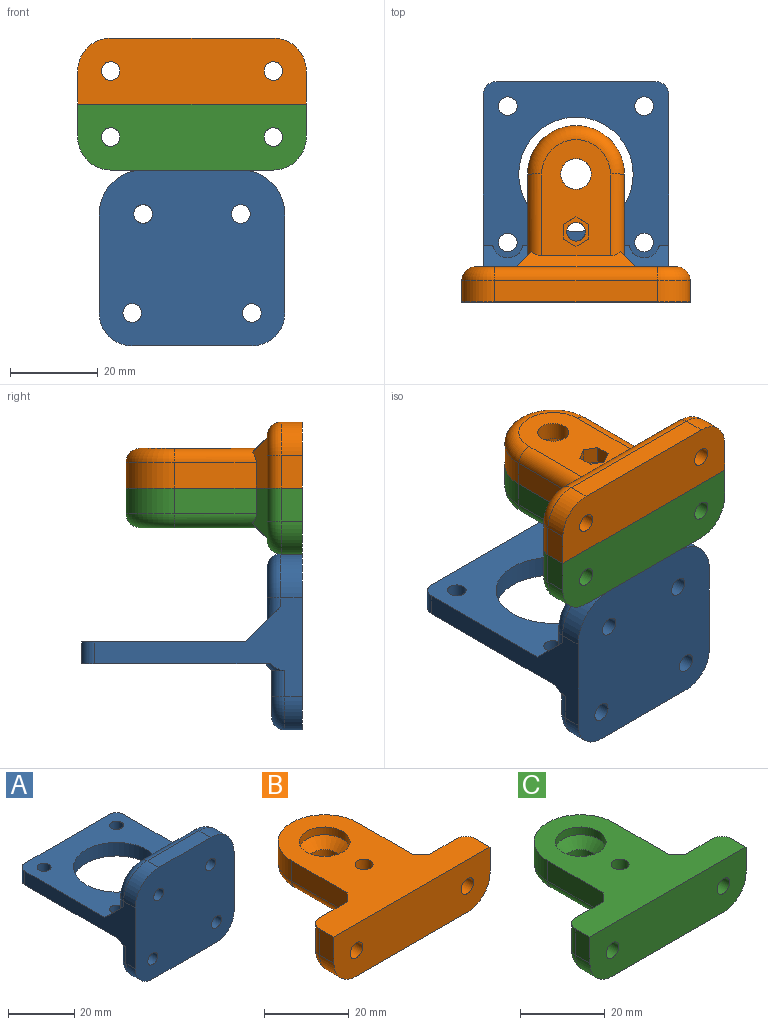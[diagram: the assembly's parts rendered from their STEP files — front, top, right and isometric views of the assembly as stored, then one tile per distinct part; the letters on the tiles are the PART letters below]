
ASSEMBLY  parts=3 mates=4
PART A: 59 faces, bbox 45.2x50.2x41.4 mm
  f0: plane 36.2x10.5mm, normal (0,1,0), area 294.4mm2, adj f27,f28,f44,f45,f46,f47,f48,f57
  f1: plane 36.2x12mm, normal (0,1,0), area 354.4mm2, adj f9,f31,f32,f33,f34,f35,f36,f37
  f2: cylinder r=2.12mm len=4.25mm, axis (0,1,0), area 53.4mm2, adj f6,f43
  f3: cylinder r=2.12mm len=4.25mm, axis (0,1,0), area 53.4mm2, adj f6,f30
  f4: cylinder r=2.12mm len=4.25mm, axis (0,1,0), area 53.4mm2, adj f6,f29
  f5: cylinder r=2.12mm len=4.25mm, axis (0,1,0), area 53.4mm2, adj f6,f26
  f6: plane 42.2x40mm, normal (0,-1,0), area 1564.2mm2, adj f2,f3,f4,f5,f10,f12,f18,f19
  f7: cylinder r=2.12mm len=5mm, axis (0,0,-1), area 66.8mm2, adj f16,f17
  f8: cylinder r=2.12mm len=5mm, axis (0,0,-1), area 66.8mm2, adj f16,f17
  f9: plane 42.2x8mm, normal (0,0.71,0.71), area 261.3mm2, adj f1,f10,f12,f16,f21,f22,f49,f53
  f10: plane 47.2x22.5mm, normal (1,0,0), area 351.2mm2, adj f6,f9,f16,f17,f19,f24,f48,f53
  f11: plane 36.2x5mm, normal (0,1,0), area 181mm2, adj f16,f17,f54,f55
  f12: plane 47.2x22.5mm, normal (-1,0,0), area 351.2mm2, adj f6,f9,f16,f17,f20,f25,f44,f49
  f13: cylinder r=13mm len=26mm, axis (0,0,-1), area 408.4mm2, adj f16,f17
  f14: cylinder r=2.12mm len=5mm, axis (0,0,-1), area 66.8mm2, adj f16,f17
  f15: cylinder r=2.12mm len=5mm, axis (0,0,-1), area 66.8mm2, adj f16,f17
  f16: plane 42.2x40.1mm, normal (0,0,1), area 1008.4mm2, adj f7,f8,f9,f10,f11,f12,f13,f14
  f17: plane 42.85x42.2mm, normal (0,0,-1), area 1170.4mm2, adj f7,f8,f10,f11,f12,f13,f14,f15
  f18: plane 22.2x5mm, normal (0,0,1), area 111mm2, adj f6,f19,f20,f51
  f19: cylinder r=10mm len=10mm, axis (0,1,0), area 78.5mm2, adj f6,f10,f18,f52
  f20: cylinder r=10mm len=10mm, axis (0,-1,0), area 78.5mm2, adj f6,f12,f18,f50
  f21: cylinder r=3.5mm len=6.9mm, axis (0,0,-1), area 18.3mm2, adj f9,f16
  f22: cylinder r=3.5mm len=6.9mm, axis (0,0,-1), area 18.3mm2, adj f9,f16
  f23: plane 27.2x4mm, normal (0,0,-1), area 108.8mm2, adj f6,f24,f25,f46
  f24: cylinder r=7.5mm len=7.5mm, axis (0,-1,0), area 47.1mm2, adj f6,f10,f23,f47
  f25: cylinder r=7.5mm len=7.5mm, axis (0,1,0), area 47.1mm2, adj f6,f12,f23,f45
  f26: plane 7x7mm, normal (0,1,0), area 24.3mm2, adj f5,f27
  f27: cylinder r=3.5mm len=7mm, axis (0,1,0), area 66mm2, adj f0,f26
  f28: cylinder r=3.5mm len=7mm, axis (0,1,0), area 66mm2, adj f0,f29
  f29: plane 7x7mm, normal (0,1,0), area 24.3mm2, adj f4,f28
  f30: plane 6.74x5.84mm, normal (0,1,0), area 15.3mm2, adj f3,f31,f32,f33,f34,f35,f36
  f31: plane 4x2.92mm, normal (-0.5,0,0.87), area 13.5mm2, adj f1,f30,f32,f36
  f32: plane 4x2.92mm, normal (0.5,0,0.87), area 13.5mm2, adj f1,f30,f31,f33
  f33: plane 4x3.37mm, normal (1,0,0), area 13.5mm2, adj f1,f30,f32,f34
  f34: plane 4x2.92mm, normal (0.5,0,-0.87), area 13.5mm2, adj f1,f30,f33,f35
  f35: plane 4x2.92mm, normal (-0.5,0,-0.87), area 13.5mm2, adj f1,f30,f34,f36
  f36: plane 4x3.37mm, normal (-1,0,0), area 13.5mm2, adj f1,f30,f31,f35
  f37: plane 4x2.92mm, normal (-0.5,0,0.87), area 13.5mm2, adj f1,f38,f42,f43
  f38: plane 4x2.92mm, normal (0.5,0,0.87), area 13.5mm2, adj f1,f37,f39,f43
  f39: plane 4x3.37mm, normal (1,0,0), area 13.5mm2, adj f1,f38,f40,f43
  f40: plane 4x2.92mm, normal (0.5,0,-0.87), area 13.5mm2, adj f1,f39,f41,f43
  f41: plane 4x2.92mm, normal (-0.5,0,-0.87), area 13.5mm2, adj f1,f40,f42,f43
  f42: plane 4x3.37mm, normal (-1,0,0), area 13.5mm2, adj f1,f37,f41,f43
  f43: plane 6.74x5.84mm, normal (0,1,0), area 15.3mm2, adj f2,f37,f38,f39,f40,f41,f42
  f44: cylinder r=3mm len=6mm, axis (0,0,1), area 28.3mm2, adj f0,f12,f45,f56
  f45: torus R=4.5mm, axis (0,1,0), area 47.4mm2, adj f0,f25,f44,f46
  f46: cylinder r=3mm len=27.2mm, axis (-1,0,0), area 128.2mm2, adj f0,f23,f45,f47
  f47: torus R=4.5mm, axis (0,1,0), area 47.4mm2, adj f0,f24,f46,f48
  f48: cylinder r=3mm len=6mm, axis (0,0,-1), area 28.3mm2, adj f0,f10,f47,f58
  f49: cylinder r=3mm len=5mm, axis (0,0,1), area 18.4mm2, adj f1,f9,f12,f50
  f50: torus R=7mm, axis (0,-1,0), area 66mm2, adj f1,f20,f49,f51
  f51: cylinder r=3mm len=22.2mm, axis (-1,0,0), area 104.6mm2, adj f1,f18,f50,f52
  f52: torus R=7mm, axis (0,-1,0), area 66mm2, adj f1,f19,f51,f53
  f53: cylinder r=3mm len=5mm, axis (0,0,-1), area 18.4mm2, adj f1,f9,f10,f52
  f54: cylinder r=3mm len=5mm, axis (0,0,-1), area 23.6mm2, adj f10,f11,f16,f17
  f55: cylinder r=3mm len=5mm, axis (0,0,1), area 23.6mm2, adj f11,f12,f16,f17
  f56: cone r=4.5mm half-angle=45deg, axis (0,0,1), area 7.6mm2, adj f12,f17,f44,f57
  f57: plane 36.2x1.5mm, normal (0,0.71,-0.71), area 76.8mm2, adj f0,f17,f56,f58
  f58: cone r=4.5mm half-angle=45deg, axis (0,0,1), area 7.6mm2, adj f10,f17,f48,f57
PART B: 50 faces, bbox 53.2x41x15.6 mm
  f0: plane 45.6x11.8mm, normal (0,1,0), area 160.7mm2, adj f18,f23,f24,f25,f28,f29,f30,f31
  f1: cylinder r=2.12mm len=4.25mm, axis (0,-1,0), area 53.4mm2, adj f12,f35
  f2: cylinder r=2.12mm len=4.25mm, axis (0,-1,0), area 53.4mm2, adj f12,f34
  f3: cylinder r=3.5mm len=7mm, axis (0,0,-1), area 93.5mm2, adj f21,f22
  f4: plane 4x2.92mm, normal (-0.5,0.87,0), area 13.5mm2, adj f5,f9,f20,f21
  f5: plane 4x2.92mm, normal (0.5,0.87,0), area 13.5mm2, adj f4,f6,f20,f21
  f6: plane 4x3.37mm, normal (1,0,0), area 13.5mm2, adj f5,f7,f20,f21
  f7: plane 4x2.92mm, normal (0.5,-0.87,0), area 13.5mm2, adj f6,f8,f20,f21
  f8: plane 4x2.92mm, normal (-0.5,-0.87,0), area 13.5mm2, adj f7,f9,f20,f21
  f9: plane 4x3.37mm, normal (-1,0,0), area 13.5mm2, adj f4,f8,f20,f21
  f10: cylinder r=2.12mm len=5mm, axis (0,0,-1), area 66.8mm2, adj f18,f20
  f11: plane 37x4.8mm, normal (0,0,-1), area 177.6mm2, adj f12,f26,f27,f44
  f12: plane 52x15mm, normal (0,-1,0), area 727.5mm2, adj f1,f2,f11,f13,f17,f18,f26,f27
  f13: plane 7.5x4.8mm, normal (1,0,0), area 36mm2, adj f12,f18,f26,f46
  f14: plane 18.6x5.8mm, normal (1,0,0), area 107.9mm2, adj f15,f18,f24,f47
  f15: cylinder r=11mm len=22mm, axis (0,0,-1), area 200.4mm2, adj f14,f16,f18,f48
  f16: plane 18.6x5.8mm, normal (-1,0,0), area 107.9mm2, adj f15,f18,f23,f49
  f17: plane 7.5x4.8mm, normal (-1,0,0), area 36mm2, adj f12,f18,f27,f42
  f18: plane 52x40.1mm, normal (0,0,1), area 944.8mm2, adj f0,f10,f12,f13,f14,f15,f16,f17
  f19: cylinder r=6mm len=12mm, axis (0,0,1), area 84.8mm2, adj f18,f22
  f20: plane 6.74x5.84mm, normal (0,0,-1), area 15.3mm2, adj f4,f5,f6,f7,f8,f9,f10
  f21: plane 26.4x15.6mm, normal (0,0,-1), area 317.8mm2, adj f3,f4,f5,f6,f7,f8,f9,f25
  f22: cone r=3.5mm half-angle=45deg, axis (0,0,1), area 105.5mm2, adj f3,f19
  f23: plane 11.5x3.44mm, normal (-0.71,0.71,0), area 37.8mm2, adj f0,f16,f18,f25,f49
  f24: plane 11.5x3.44mm, normal (0.71,0.71,0), area 37.8mm2, adj f0,f14,f18,f25,f47
  f25: plane 27x3.44mm, normal (0,0.71,-0.71), area 89.7mm2, adj f0,f21,f23,f24,f47,f49
  f26: cylinder r=7.5mm len=7.5mm, axis (0,1,0), area 56.5mm2, adj f11,f12,f13,f45
  f27: cylinder r=7.5mm len=7.5mm, axis (0,-1,0), area 56.5mm2, adj f11,f12,f17,f43
  f28: plane 4x3.37mm, normal (-1,0,0), area 13.5mm2, adj f0,f29,f33,f34
  f29: plane 4x2.92mm, normal (-0.5,0,0.87), area 13.5mm2, adj f0,f28,f30,f34
  f30: plane 4x2.92mm, normal (0.5,0,0.87), area 13.5mm2, adj f0,f29,f31,f34
  f31: plane 4x3.37mm, normal (1,0,0), area 13.5mm2, adj f0,f30,f32,f34
  f32: plane 4x2.92mm, normal (0.5,0,-0.87), area 13.5mm2, adj f0,f31,f33,f34
  f33: plane 4x2.92mm, normal (-0.5,0,-0.87), area 13.5mm2, adj f0,f28,f32,f34
  f34: plane 6.74x5.84mm, normal (0,1,0), area 15.3mm2, adj f2,f28,f29,f30,f31,f32,f33
  f35: plane 6.74x5.84mm, normal (0,1,0), area 15.3mm2, adj f1,f36,f37,f38,f39,f40,f41
  f36: plane 4x2.92mm, normal (-0.5,0,0.87), area 13.5mm2, adj f0,f35,f37,f41
  f37: plane 4x2.92mm, normal (0.5,0,0.87), area 13.5mm2, adj f0,f35,f36,f38
  f38: plane 4x3.37mm, normal (1,0,0), area 13.5mm2, adj f0,f35,f37,f39
  f39: plane 4x2.92mm, normal (0.5,0,-0.87), area 13.5mm2, adj f0,f35,f38,f40
  f40: plane 4x2.92mm, normal (-0.5,0,-0.87), area 13.5mm2, adj f0,f35,f39,f41
  f41: plane 4x3.37mm, normal (-1,0,0), area 13.5mm2, adj f0,f35,f36,f40
  f42: cylinder r=3.2mm len=7.5mm, axis (0,0,-1), area 37.7mm2, adj f0,f17,f18,f43
  f43: torus R=4.3mm, axis (0,-1,0), area 50mm2, adj f0,f27,f42,f44
  f44: cylinder r=3.2mm len=37mm, axis (-1,0,0), area 186mm2, adj f0,f11,f43,f45
  f45: torus R=4.3mm, axis (0,-1,0), area 50mm2, adj f0,f26,f44,f46
  f46: cylinder r=3.2mm len=7.5mm, axis (0,0,1), area 37.7mm2, adj f0,f13,f18,f45
  f47: cylinder r=3.2mm len=18.6mm, axis (0,-1,0), area 91.9mm2, adj f14,f21,f24,f25,f48
  f48: torus R=7.8mm, axis (0,0,-1), area 155.3mm2, adj f15,f21,f47,f49
  f49: cylinder r=3.2mm len=18.6mm, axis (0,1,0), area 91.9mm2, adj f16,f21,f23,f25,f48
PART C: 45 faces, bbox 53.2x41x15.6 mm
  f0: plane 45.6x11.8mm, normal (0,1,0), area 160.7mm2, adj f12,f18,f19,f20,f23,f24,f25,f26
  f1: cylinder r=2.12mm len=4.25mm, axis (0,-1,0), area 53.4mm2, adj f6,f30
  f2: cylinder r=2.12mm len=4.25mm, axis (0,-1,0), area 53.4mm2, adj f6,f29
  f3: cylinder r=3.5mm len=7mm, axis (0,0,-1), area 93.5mm2, adj f16,f17
  f4: cylinder r=3.5mm len=7mm, axis (0,0,-1), area 88mm2, adj f15,f16
  f5: cylinder r=2.12mm len=5mm, axis (0,0,-1), area 66.8mm2, adj f12,f15
  f6: plane 52x15mm, normal (0,-1,0), area 727.5mm2, adj f1,f2,f7,f11,f12,f13,f21,f22
  f7: plane 7.5x4.8mm, normal (1,0,0), area 36mm2, adj f6,f12,f21,f41
  f8: plane 18.6x5.8mm, normal (1,0,0), area 107.9mm2, adj f9,f12,f19,f42
  f9: cylinder r=11mm len=22mm, axis (0,0,-1), area 200.4mm2, adj f8,f10,f12,f43
  f10: plane 18.6x5.8mm, normal (-1,0,0), area 107.9mm2, adj f9,f12,f18,f44
  f11: plane 7.5x4.8mm, normal (-1,0,0), area 36mm2, adj f6,f12,f22,f37
  f12: plane 52x40.1mm, normal (0,0,1), area 944.8mm2, adj f0,f5,f6,f7,f8,f9,f10,f11
  f13: plane 37x4.8mm, normal (0,0,-1), area 177.6mm2, adj f6,f21,f22,f39
  f14: cylinder r=6mm len=12mm, axis (0,0,1), area 84.8mm2, adj f12,f17
  f15: plane 7x7mm, normal (0,0,-1), area 24.3mm2, adj f4,f5
  f16: plane 26.4x15.6mm, normal (0,0,-1), area 308.8mm2, adj f3,f4,f20,f42,f43,f44
  f17: cone r=3.5mm half-angle=45deg, axis (0,0,1), area 105.5mm2, adj f3,f14
  f18: plane 11.5x3.44mm, normal (-0.71,0.71,0), area 37.8mm2, adj f0,f10,f12,f20,f44
  f19: plane 11.5x3.44mm, normal (0.71,0.71,0), area 37.8mm2, adj f0,f8,f12,f20,f42
  f20: plane 27x3.44mm, normal (0,0.71,-0.71), area 89.7mm2, adj f0,f16,f18,f19,f42,f44
  f21: cylinder r=7.5mm len=7.5mm, axis (0,1,0), area 56.5mm2, adj f6,f7,f13,f40
  f22: cylinder r=7.5mm len=7.5mm, axis (0,-1,0), area 56.5mm2, adj f6,f11,f13,f38
  f23: plane 4x3.37mm, normal (-1,0,0), area 13.5mm2, adj f0,f24,f28,f29
  f24: plane 4x2.92mm, normal (-0.5,0,0.87), area 13.5mm2, adj f0,f23,f25,f29
  f25: plane 4x2.92mm, normal (0.5,0,0.87), area 13.5mm2, adj f0,f24,f26,f29
  f26: plane 4x3.37mm, normal (1,0,0), area 13.5mm2, adj f0,f25,f27,f29
  f27: plane 4x2.92mm, normal (0.5,0,-0.87), area 13.5mm2, adj f0,f26,f28,f29
  f28: plane 4x2.92mm, normal (-0.5,0,-0.87), area 13.5mm2, adj f0,f23,f27,f29
  f29: plane 6.74x5.84mm, normal (0,1,0), area 15.3mm2, adj f2,f23,f24,f25,f26,f27,f28
  f30: plane 6.74x5.84mm, normal (0,1,0), area 15.3mm2, adj f1,f31,f32,f33,f34,f35,f36
  f31: plane 4x2.92mm, normal (-0.5,0,0.87), area 13.5mm2, adj f0,f30,f32,f36
  f32: plane 4x2.92mm, normal (0.5,0,0.87), area 13.5mm2, adj f0,f30,f31,f33
  f33: plane 4x3.37mm, normal (1,0,0), area 13.5mm2, adj f0,f30,f32,f34
  f34: plane 4x2.92mm, normal (0.5,0,-0.87), area 13.5mm2, adj f0,f30,f33,f35
  f35: plane 4x2.92mm, normal (-0.5,0,-0.87), area 13.5mm2, adj f0,f30,f34,f36
  f36: plane 4x3.37mm, normal (-1,0,0), area 13.5mm2, adj f0,f30,f31,f35
  f37: cylinder r=3.2mm len=7.5mm, axis (0,0,-1), area 37.7mm2, adj f0,f11,f12,f38
  f38: torus R=4.3mm, axis (0,-1,0), area 50mm2, adj f0,f22,f37,f39
  f39: cylinder r=3.2mm len=37mm, axis (-1,0,0), area 186mm2, adj f0,f13,f38,f40
  f40: torus R=4.3mm, axis (0,-1,0), area 50mm2, adj f0,f21,f39,f41
  f41: cylinder r=3.2mm len=7.5mm, axis (0,0,1), area 37.7mm2, adj f0,f7,f12,f40
  f42: cylinder r=3.2mm len=18.6mm, axis (0,-1,0), area 91.9mm2, adj f8,f16,f19,f20,f43
  f43: torus R=7.8mm, axis (0,0,-1), area 155.3mm2, adj f9,f16,f42,f44
  f44: cylinder r=3.2mm len=18.6mm, axis (0,1,0), area 91.9mm2, adj f10,f16,f18,f20,f43
PLACE A rot(axis=(-0.04,0.22,0.97),0deg) t=(-55.03,-13.52,40.43)mm
PLACE B rot(axis=(0,-1,0),180deg) t=(-55.03,-42.62,95.43)mm
PLACE C rot(axis=(-0.83,0.54,0.15),0deg) t=(-55.03,-42.62,65.43)mm
MATE cylindrical A.f13 <-> B.f3  axis (0,0,-1) through (-55.03,-13.52,42.93)mm
MATE cylindrical C.f3 <-> B.f3  axis (0,0,-1) through (-55.03,-13.52,73.56)mm
MATE planar C.f12 <-> B.f18  axis (0,0,1) through (-55.03,-28.66,80.43)mm
MATE planar C.f13 <-> A.f18  axis (0,0,-1) through (-55.03,-40.22,65.43)mm
